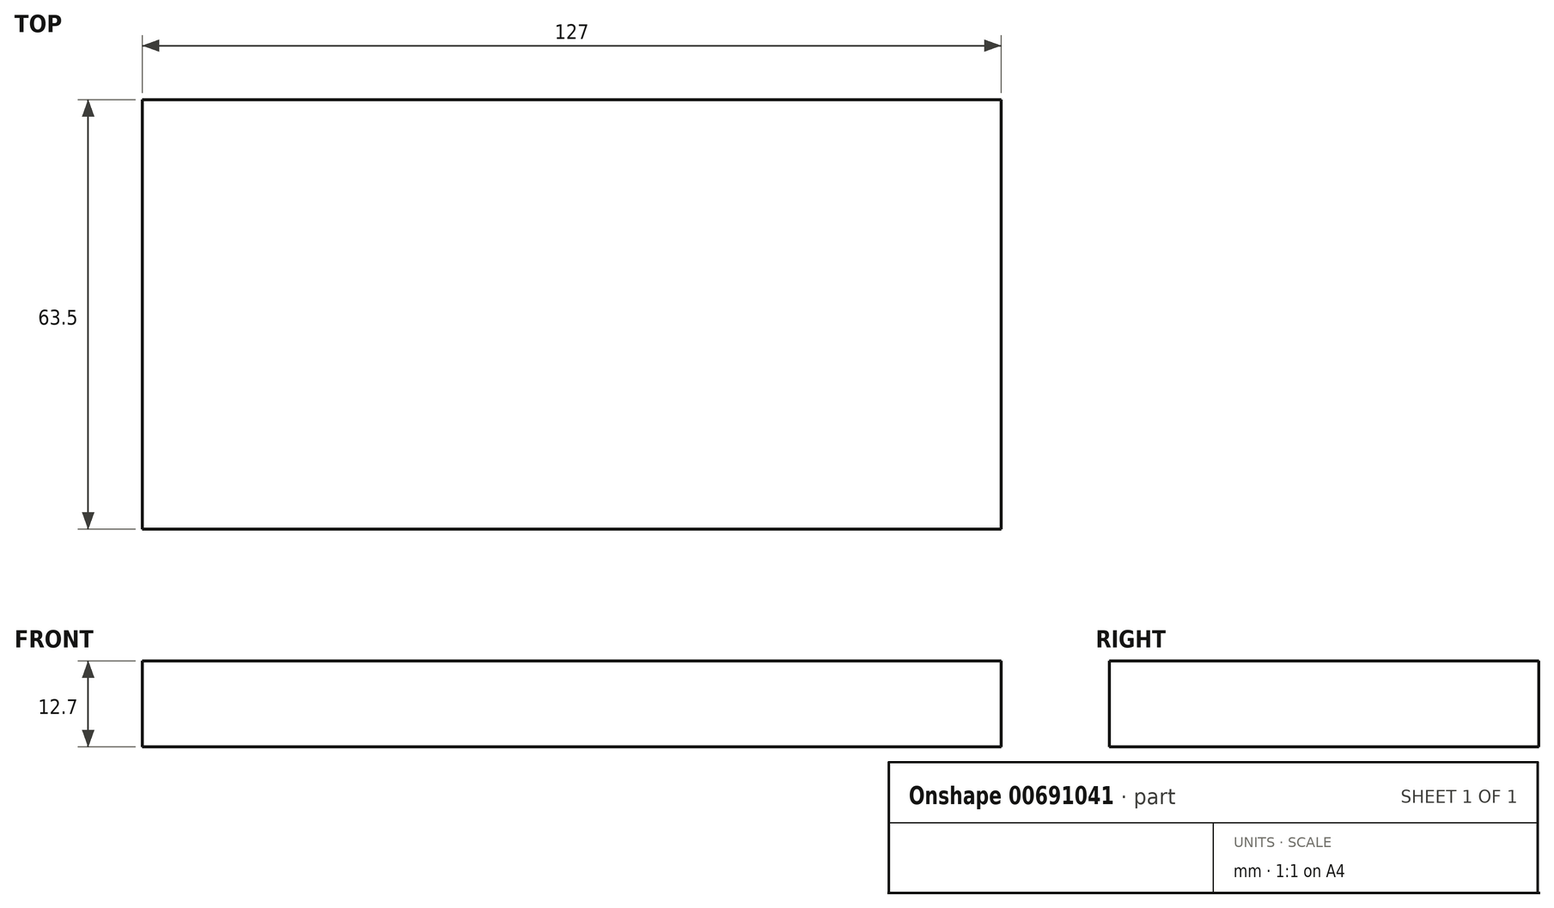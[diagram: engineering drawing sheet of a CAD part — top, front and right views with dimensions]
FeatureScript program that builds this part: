
annotation { "Feature Type Name" : "Feature", "Feature Type Description" : "" }
export const myFeature = defineFeature(function(context is Context, id is Id, definition is map)
    precondition{}
    {
        {
            var Q0;
            Q0=qCreatedBy(makeId("Top.planeOp"),FACE);
            var sketch = newSketch(context, id + "F0", { "sketchPlane" : qUnion([Q0])});
            skLineSegment(sketch, "E0.bottom", {"start": v(-63.38, 29.19) * mm, "end": v(63.62, 29.19) * mm});
            skLineSegment(sketch, "E0.top", {"start": v(-63.38, -34.31) * mm, "end": v(63.62, -34.31) * mm});
            skLineSegment(sketch, "E0.left", {"start": v(-63.38, 29.19) * mm, "end": v(-63.38, -34.31) * mm});
            skLineSegment(sketch, "E0.right", {"start": v(63.62, 29.19) * mm, "end": v(63.62, -34.31) * mm});
            skSolve(sketch);
        }
        {
            var Q0;
            Q0=makeQuery(id+"F0.imprint","IMPRINT",FACE,{"disambiguationData":[TD([[makeQuery(id+"F0.imprint","IMPRINT",EDGE,{"derivedFrom":sQuery(id+"F0.wireOp",EDGE,"E0.bottom")}),-1.0]])]});
            extrude(context, id + "F1", {"entities" : qUnion([Q0]), "depth" : 12.7 * mm, "offsetDistance" : 25.4 * mm});
        }
    });
